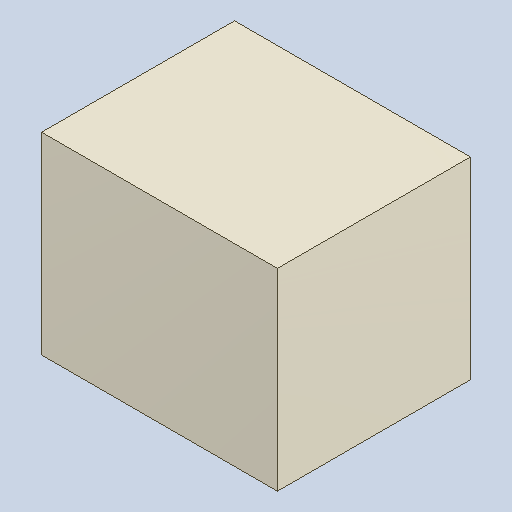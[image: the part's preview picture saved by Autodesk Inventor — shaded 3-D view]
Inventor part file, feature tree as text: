
AUTODESK INVENTOR PART (.ipt)
format: ipt  version: 2023.4 (Build 274418000, 418)  size: 81,920 bytes
history: native  units: mm
features: extrude x1
ambient origin geometry x8: Origin, YZ Plane, XZ Plane, XY Plane, X Axis, Y Axis, Z Axis, Center Point
bodies: Solid1 (feature_tree)
feature tree (1):
  extrude  "Extruded_13"  [1 undecoded]
note: 1 required parameter value undecoded (feature->parameter linkage not recoverable at this tier; creation-order binding heuristic only, values carry confidence <= 0.55)
